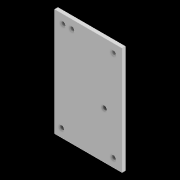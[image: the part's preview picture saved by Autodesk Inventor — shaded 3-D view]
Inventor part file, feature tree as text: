
AUTODESK INVENTOR PART (.ipt)
format: ipt  version: 2020 (Build 240168000, 168)  size: 99,328 bytes
history: native  units: mm
features: sketch x3, hole x2, extrude x1
ambient origin geometry x8: Origin, YZ Plane, XZ Plane, XY Plane, X Axis, Y Axis, Z Axis, Center Point
bodies: Solid1 (feature_tree)
feature tree (6):
  extrude  "Extrusion1"  Depth=79.0mm
  hole  "Hole1"  [1 undecoded]
  hole  "Hole2"  [1 undecoded]
  sketch  "Sketch1"  dims[d0=49.5mm d1=79.0mm]
  sketch  "Sketch2"  dims[d2=2.5mm d3=0.0mm d4=12.777mm]
  sketch  "Sketch3"  dims[d5=6.265mm d6=38.329mm d7=23.774mm d8=3.3mm d9=6.0mm d10=4.0mm d11=2.0mm d12=90.0deg d13=8.0mm d14=20.594885mm d15=6.25mm d16=5.25mm d17=38.0mm d18=72.75mm d19=3.3mm d20=6.0mm d21=4.0mm d22=2.0mm d23=90.0deg d24=8.0mm d25=20.594885mm d26=6.25mm]
note: 2 required parameter values undecoded (feature->parameter linkage not recoverable at this tier; creation-order binding heuristic only, values carry confidence <= 0.55)
